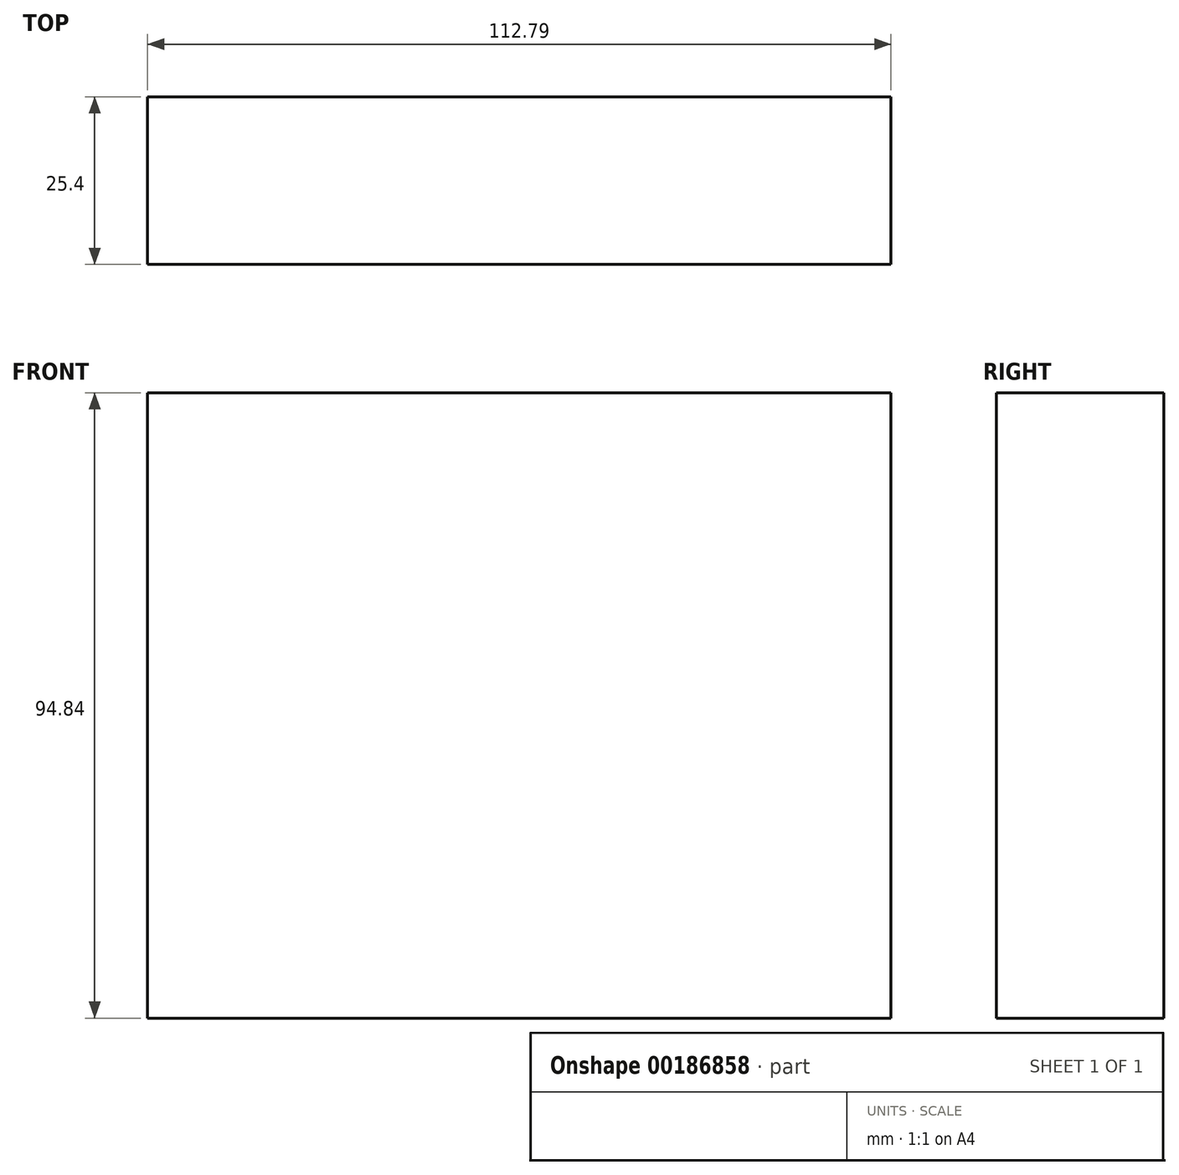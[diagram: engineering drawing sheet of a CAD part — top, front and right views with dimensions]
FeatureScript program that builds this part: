
annotation { "Feature Type Name" : "Feature", "Feature Type Description" : "" }
export const myFeature = defineFeature(function(context is Context, id is Id, definition is map)
    precondition{}
    {
        {
            var Q0;
            Q0=qCreatedBy(makeId("Front.planeOp"),FACE);
            var sketch = newSketch(context, id + "F0", { "sketchPlane" : qUnion([Q0])});
            skLineSegment(sketch, "E0", {"start": v(-203.67, -59.58) * mm, "end": v(-203.67, 35.26) * mm});
            skLineSegment(sketch, "E1", {"start": v(-203.67, 35.26) * mm, "end": v(-90.88, 35.26) * mm});
            skLineSegment(sketch, "E2", {"start": v(-90.88, 35.26) * mm, "end": v(-90.88, -59.58) * mm});
            skLineSegment(sketch, "E3", {"start": v(-90.88, -59.58) * mm, "end": v(-203.67, -59.58) * mm});
            skSolve(sketch);
        }
        {
            var Q0;
            Q0=makeQuery(id+"F0.imprint","IMPRINT",FACE,{"disambiguationData":[TD([[makeQuery(id+"F0.imprint","IMPRINT",EDGE,{"derivedFrom":sQuery(id+"F0.wireOp",EDGE,"E0")}),-1.0]])]});
            extrude(context, id + "F1", {"entities" : qUnion([Q0]), "depth" : 25.4 * mm});
        }
    });
